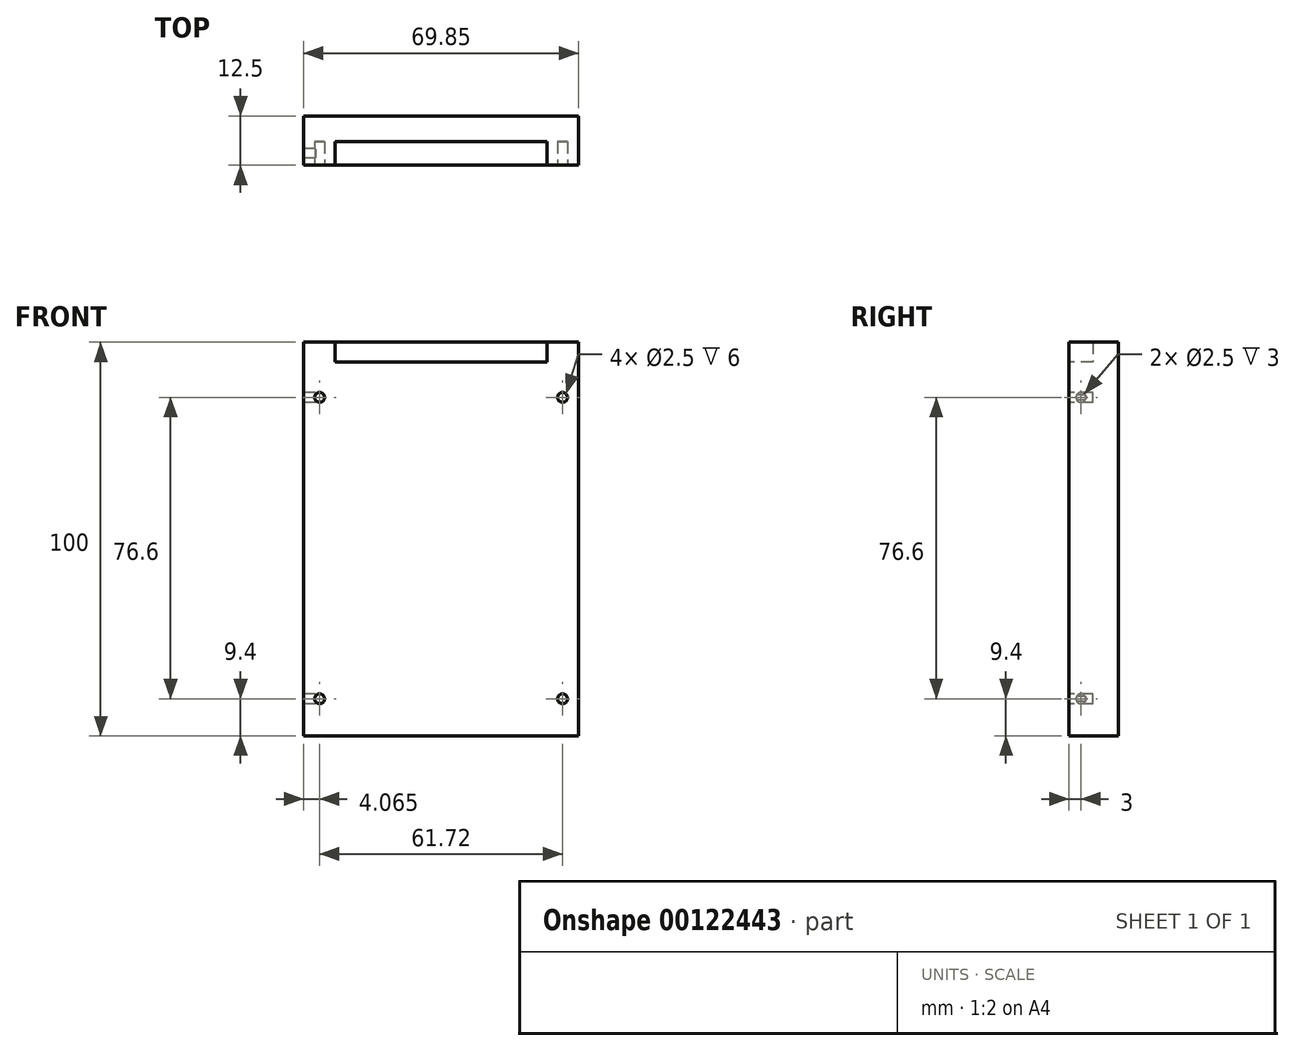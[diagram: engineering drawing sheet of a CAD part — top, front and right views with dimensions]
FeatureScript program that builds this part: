
annotation { "Feature Type Name" : "Feature", "Feature Type Description" : "" }
export const myFeature = defineFeature(function(context is Context, id is Id, definition is map)
    precondition{}
    {
        {
            var Q0;
            Q0=qCreatedBy(makeId("Front.planeOp"),FACE);
            var sketch = newSketch(context, id + "F0", { "sketchPlane" : qUnion([Q0])});
            skLineSegment(sketch, "E0.bottom", {"start": v(0, 0) * mm, "end": v(69.85, 0) * mm});
            skLineSegment(sketch, "E0.top", {"start": v(0, 100) * mm, "end": v(69.85, 100) * mm});
            skLineSegment(sketch, "E0.left", {"start": v(0, 0) * mm, "end": v(0, 100) * mm});
            skLineSegment(sketch, "E0.right", {"start": v(69.85, 0) * mm, "end": v(69.85, 100) * mm});
            skSolve(sketch);
        }
        {
            var Q0;
            Q0 = qSketchRegion(id + "F0", true);
            extrude(context, id + "F1", {"entities" : qUnion([Q0]), "depth" : 12.5 * mm});
        }
        {
            var Q0;
            Q0=makeQuery(id+"F1.opExtrude","CAP_FACE",FACE,{"disambiguationData":[OSD([sQuery(id+"F0.wireOp",EDGE,"E0.bottom"),sQuery(id+"F0.wireOp",EDGE,"E0.top"),sQuery(id+"F0.wireOp",EDGE,"E0.left"),sQuery(id+"F0.wireOp",EDGE,"E0.right")])],"isStart":false});
            var sketch = newSketch(context, id + "F2", { "sketchPlane" : qUnion([Q0])});
            skCircle(sketch, "E1", {"center": v(4.07, 9.4) * mm, "radius": 1.25 * mm});
            skCircle(sketch, "E2", {"center": v(4.06, 86) * mm, "radius": 1.25 * mm});
            skLineSegment(sketch, "E3", {"start": v(34.92, 100) * mm, "end": v(34.92, 0) * mm, "construction": true});
            skCircle(sketch, "E4.MirrorC", {"center": v(65.78, 9.4) * mm, "radius": 1.25 * mm});
            skCircle(sketch, "E5.MirrorC", {"center": v(65.78, 86) * mm, "radius": 1.25 * mm});
            skLineSegment(sketch, "E6.bottom", {"start": v(8, 100) * mm, "end": v(61.85, 100) * mm});
            skLineSegment(sketch, "E6.top", {"start": v(8, 95) * mm, "end": v(61.85, 95) * mm});
            skLineSegment(sketch, "E6.left", {"start": v(8, 100) * mm, "end": v(8, 95) * mm});
            skLineSegment(sketch, "E6.right", {"start": v(61.85, 100) * mm, "end": v(61.85, 95) * mm});
            skSolve(sketch);
        }
        {
            var Q0;
            Q0 = qSketchRegion(id + "F2", true);
            extrude(context, id + "F3", {"entities" : qUnion([Q0]), "operationType" : NewBodyOperationType.REMOVE, "oppositeDirection" : true, "depth" : 6 * mm});
        }
        {
            var Q0;
            Q0=makeQuery(id+"F1.opExtrude","SWEPT_FACE",FACE,{"disambiguationData":[OSD([sQuery(id+"F0.wireOp",EDGE,"E0.left")])]});
            var sketch = newSketch(context, id + "F4", { "sketchPlane" : qUnion([Q0])});
            skCircle(sketch, "E7", {"center": v(9.5, 86) * mm, "radius": 1.25 * mm});
            skCircle(sketch, "E8", {"center": v(9.5, 9.4) * mm, "radius": 1.25 * mm});
            skSolve(sketch);
        }
        {
            var Q0;
            Q0 = qSketchRegion(id + "F4", true);
            extrude(context, id + "F5", {"entities" : qUnion([Q0]), "operationType" : NewBodyOperationType.REMOVE, "oppositeDirection" : true, "depth" : 3 * mm});
        }
        {
            var Q0;
            Q0=makeQuery(id+"F1.opExtrude","SWEPT_FACE",FACE,{"disambiguationData":[OSD([sQuery(id+"F0.wireOp",EDGE,"E0.left")])]});
            var Q1;
            Q1=makeQuery(id+"F1.opExtrude","SWEPT_FACE",FACE,{"disambiguationData":[OSD([sQuery(id+"F0.wireOp",EDGE,"E0.right")])]});
            cPlane(context, id + "F6", {"entities" : qUnion([Q0, Q1]), "cplaneType" : CPlaneType.MID_PLANE, "offset" : 25 * mm, "width" : 150 * mm, "height" : 150 * mm});
        }
    });
